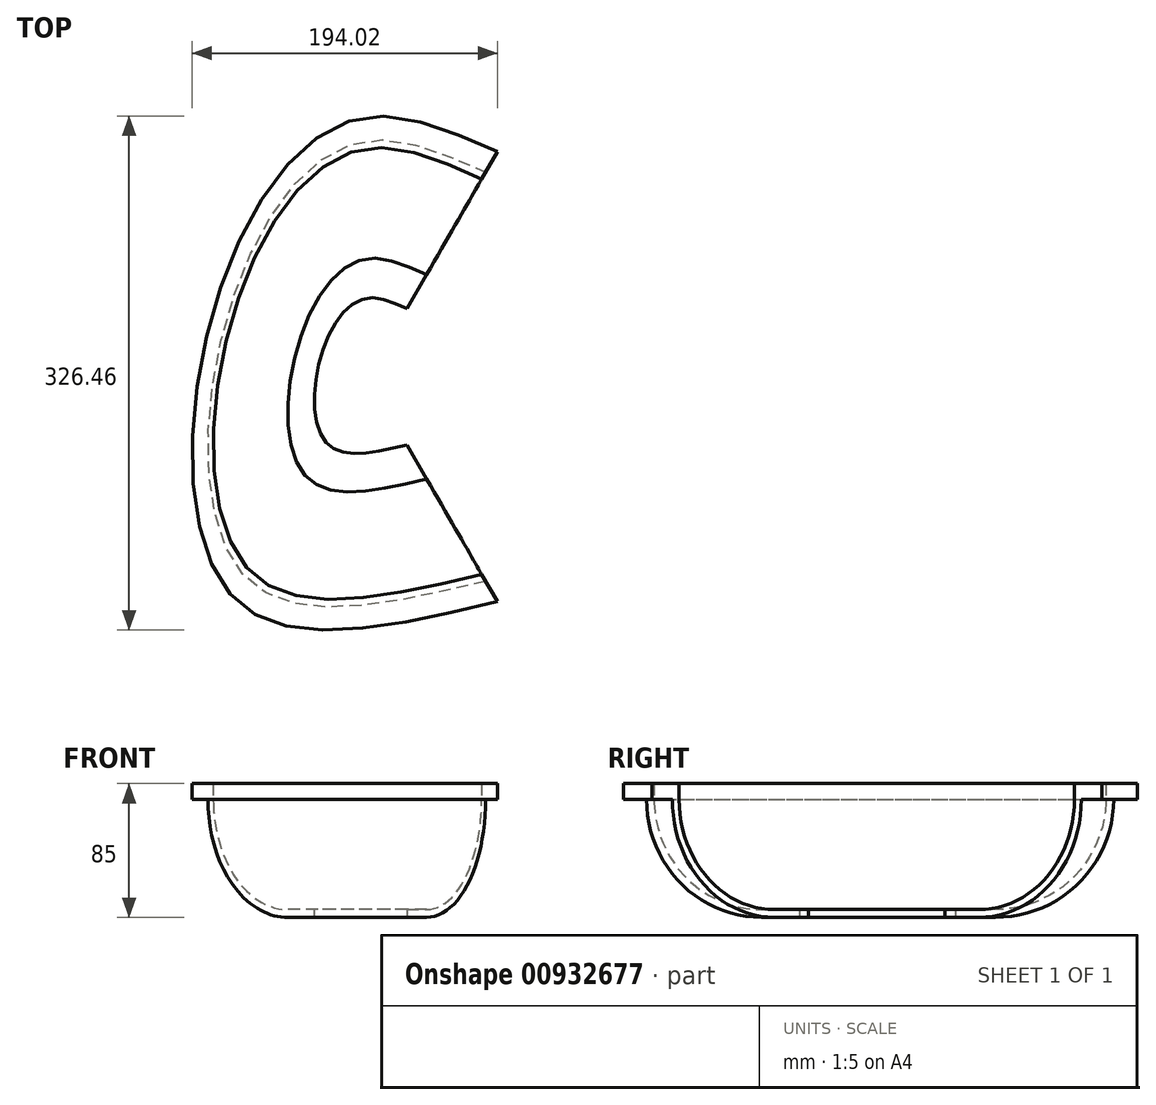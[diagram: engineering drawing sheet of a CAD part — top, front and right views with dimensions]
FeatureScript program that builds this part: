
annotation { "Feature Type Name" : "Feature", "Feature Type Description" : "" }
export const myFeature = defineFeature(function(context is Context, id is Id, definition is map)
    precondition{}
    {
        {
            var Q0;
            Q0=qCreatedBy(makeId("Right.planeOp"),FACE);
            var sketch = newSketch(context, id + "F0", { "sketchPlane" : qUnion([Q0])});
            skLineSegment(sketch, "E0.bottom", {"start": v(50, -45) * mm, "end": v(75, -45) * mm});
            skLineSegment(sketch, "E0.top", {"start": v(50, -50) * mm, "end": v(75, -50) * mm});
            skLineSegment(sketch, "E0.left", {"start": v(50, -45) * mm, "end": v(50, -50) * mm});
            skLineSegment(sketch, "E0.right", {"start": v(75, -45) * mm, "end": v(75, -50) * mm, "construction": true});
            skLineSegment(sketch, "E1.bottom", {"start": v(145, 35) * mm, "end": v(165, 35) * mm});
            skLineSegment(sketch, "E1.top", {"start": v(150, 25) * mm, "end": v(165, 25) * mm});
            skLineSegment(sketch, "E1.left", {"start": v(145, 35) * mm, "end": v(145, 25) * mm});
            skLineSegment(sketch, "E1.right", {"start": v(165, 35) * mm, "end": v(165, 25) * mm});
            skArc(sketch, "E2", {"start": v(75, -50) * mm, "mid": v(128.03, -28.03) * mm, "end": v(150, 25) * mm});
            skArc(sketch, "E3", {"start": v(75, -45) * mm, "mid": v(124.5, -24.5) * mm, "end": v(145, 25) * mm});
            skLineSegment(sketch, "E4", {"start": v(0, 0) * mm, "end": v(0, -50) * mm, "construction": true});
            skSolve(sketch);
        }
        {
            var Q0;
            Q0=sQuery(id+"F0.wireOp",EDGE,"E4");
            cPlane(context, id + "F1", {"entities" : qUnion([Q0]), "cplaneType" : CPlaneType.LINE_ANGLE, "offset" : 25 * mm, "angle" : 30 * degree, "width" : 150 * mm, "height" : 150 * mm});
        }
        {
            var Q0;
            Q0=qCreatedBy(id+"F1.planeOp",FACE);
            var sketch = newSketch(context, id + "F2", { "sketchPlane" : qUnion([Q0])});
            skLineSegment(sketch, "E5.bottom", {"start": v(50, -45) * mm, "end": v(75, -45) * mm});
            skLineSegment(sketch, "E5.top", {"start": v(50, -50) * mm, "end": v(75, -50) * mm});
            skLineSegment(sketch, "E5.left", {"start": v(50, -45) * mm, "end": v(50, -50) * mm});
            skLineSegment(sketch, "E5.right", {"start": v(75, -45) * mm, "end": v(75, -50) * mm, "construction": true});
            skLineSegment(sketch, "E6.bottom", {"start": v(145, 35) * mm, "end": v(165, 35) * mm});
            skLineSegment(sketch, "E6.top", {"start": v(150, 25) * mm, "end": v(165, 25) * mm});
            skLineSegment(sketch, "E6.left", {"start": v(145, 35) * mm, "end": v(145, 25) * mm});
            skLineSegment(sketch, "E6.right", {"start": v(165, 35) * mm, "end": v(165, 25) * mm});
            skArc(sketch, "E7", {"start": v(75, -50) * mm, "mid": v(128.03, -28.03) * mm, "end": v(150, 25) * mm});
            skArc(sketch, "E8", {"start": v(75, -45) * mm, "mid": v(124.5, -24.5) * mm, "end": v(145, 25) * mm});
            skLineSegment(sketch, "E9", {"start": v(0, 0) * mm, "end": v(0, -50) * mm, "construction": true});
            skSolve(sketch);
        }
        {
            var Q0;
            Q0=sQuery(id+"F2.wireOp",EDGE,"E9");
            cPlane(context, id + "F3", {"entities" : qUnion([Q0]), "cplaneType" : CPlaneType.LINE_ANGLE, "offset" : 25 * mm, "angle" : 330 * degree, "width" : 150 * mm, "height" : 150 * mm});
        }
        {
            var Q0;
            Q0=qCreatedBy(id+"F3.planeOp",FACE);
            var sketch = newSketch(context, id + "F4", { "sketchPlane" : qUnion([Q0])});
            skLineSegment(sketch, "E10.bottom", {"start": v(50, -45) * mm, "end": v(75, -45) * mm});
            skLineSegment(sketch, "E10.top", {"start": v(50, -50) * mm, "end": v(75, -50) * mm});
            skLineSegment(sketch, "E10.left", {"start": v(50, -45) * mm, "end": v(50, -50) * mm});
            skLineSegment(sketch, "E10.right", {"start": v(75, -45) * mm, "end": v(75, -50) * mm, "construction": true});
            skLineSegment(sketch, "E11.bottom", {"start": v(145, 35) * mm, "end": v(165, 35) * mm});
            skLineSegment(sketch, "E11.top", {"start": v(150, 25) * mm, "end": v(165, 25) * mm});
            skLineSegment(sketch, "E11.left", {"start": v(145, 35) * mm, "end": v(145, 25) * mm});
            skLineSegment(sketch, "E11.right", {"start": v(165, 35) * mm, "end": v(165, 25) * mm});
            skArc(sketch, "E12", {"start": v(75, -50) * mm, "mid": v(128.03, -28.03) * mm, "end": v(150, 25) * mm});
            skArc(sketch, "E13", {"start": v(75, -45) * mm, "mid": v(124.5, -24.5) * mm, "end": v(145, 25) * mm});
            skLineSegment(sketch, "E14", {"start": v(0, 0) * mm, "end": v(0, -50) * mm, "construction": true});
            skSolve(sketch);
        }
        {
            var Q0;
            Q0=sQuery(id+"F2.wireOp",EDGE,"E9");
            cPlane(context, id + "F5", {"entities" : qUnion([Q0]), "cplaneType" : CPlaneType.LINE_ANGLE, "offset" : 25 * mm, "angle" : 150 * degree, "oppositeDirection" : true, "width" : 150 * mm, "height" : 150 * mm});
        }
        {
            var Q0;
            Q0=qCreatedBy(id+"F5.planeOp",FACE);
            var sketch = newSketch(context, id + "F6", { "sketchPlane" : qUnion([Q0])});
            skLineSegment(sketch, "E15.bottom", {"start": v(50, -45) * mm, "end": v(75, -45) * mm});
            skLineSegment(sketch, "E15.top", {"start": v(50, -50) * mm, "end": v(75, -50) * mm});
            skLineSegment(sketch, "E15.left", {"start": v(50, -45) * mm, "end": v(50, -50) * mm});
            skLineSegment(sketch, "E15.right", {"start": v(75, -45) * mm, "end": v(75, -50) * mm, "construction": true});
            skLineSegment(sketch, "E16.bottom", {"start": v(145, 35) * mm, "end": v(165, 35) * mm});
            skLineSegment(sketch, "E16.top", {"start": v(150, 25) * mm, "end": v(165, 25) * mm});
            skLineSegment(sketch, "E16.left", {"start": v(145, 35) * mm, "end": v(145, 25) * mm});
            skLineSegment(sketch, "E16.right", {"start": v(165, 35) * mm, "end": v(165, 25) * mm});
            skArc(sketch, "E17", {"start": v(75, -50) * mm, "mid": v(128.03, -28.03) * mm, "end": v(150, 25) * mm});
            skArc(sketch, "E18", {"start": v(75, -45) * mm, "mid": v(124.5, -24.5) * mm, "end": v(145, 25) * mm});
            skLineSegment(sketch, "E19", {"start": v(0, 0) * mm, "end": v(0, -50) * mm, "construction": true});
            skSolve(sketch);
        }
        {
            var Q0;
            Q0=makeQuery(id+"F4.imprint","IMPRINT",FACE,{"disambiguationData":[TD([[makeQuery(id+"F4.imprint","IMPRINT",EDGE,{"derivedFrom":sQuery(id+"F4.wireOp",EDGE,"E10.bottom")}),-1.0]])]});
            var Q1;
            Q1=makeQuery(id+"F2.imprint","IMPRINT",FACE,{"disambiguationData":[TD([[makeQuery(id+"F2.imprint","IMPRINT",EDGE,{"derivedFrom":sQuery(id+"F2.wireOp",EDGE,"E5.bottom")}),-1.0]])]});
            var Q2;
            Q2=makeQuery(id+"F0.imprint","IMPRINT",FACE,{"disambiguationData":[TD([[makeQuery(id+"F0.imprint","IMPRINT",EDGE,{"derivedFrom":sQuery(id+"F0.wireOp",EDGE,"E0.bottom")}),-1.0]])]});
            var Q3;
            Q3=makeQuery(id+"F6.imprint","IMPRINT",FACE,{"disambiguationData":[TD([[makeQuery(id+"F6.imprint","IMPRINT",EDGE,{"derivedFrom":sQuery(id+"F6.wireOp",EDGE,"E15.bottom")}),-1.0]])]});
            loft(context, id + "F7", {"sheetProfilesArray" : [{ "sheetProfileEntities" : qUnion([Q0]) }, { "sheetProfileEntities" : qUnion([Q1]) }, { "sheetProfileEntities" : qUnion([Q2]) }, { "sheetProfileEntities" : qUnion([Q3]) }]});
        }
    });
